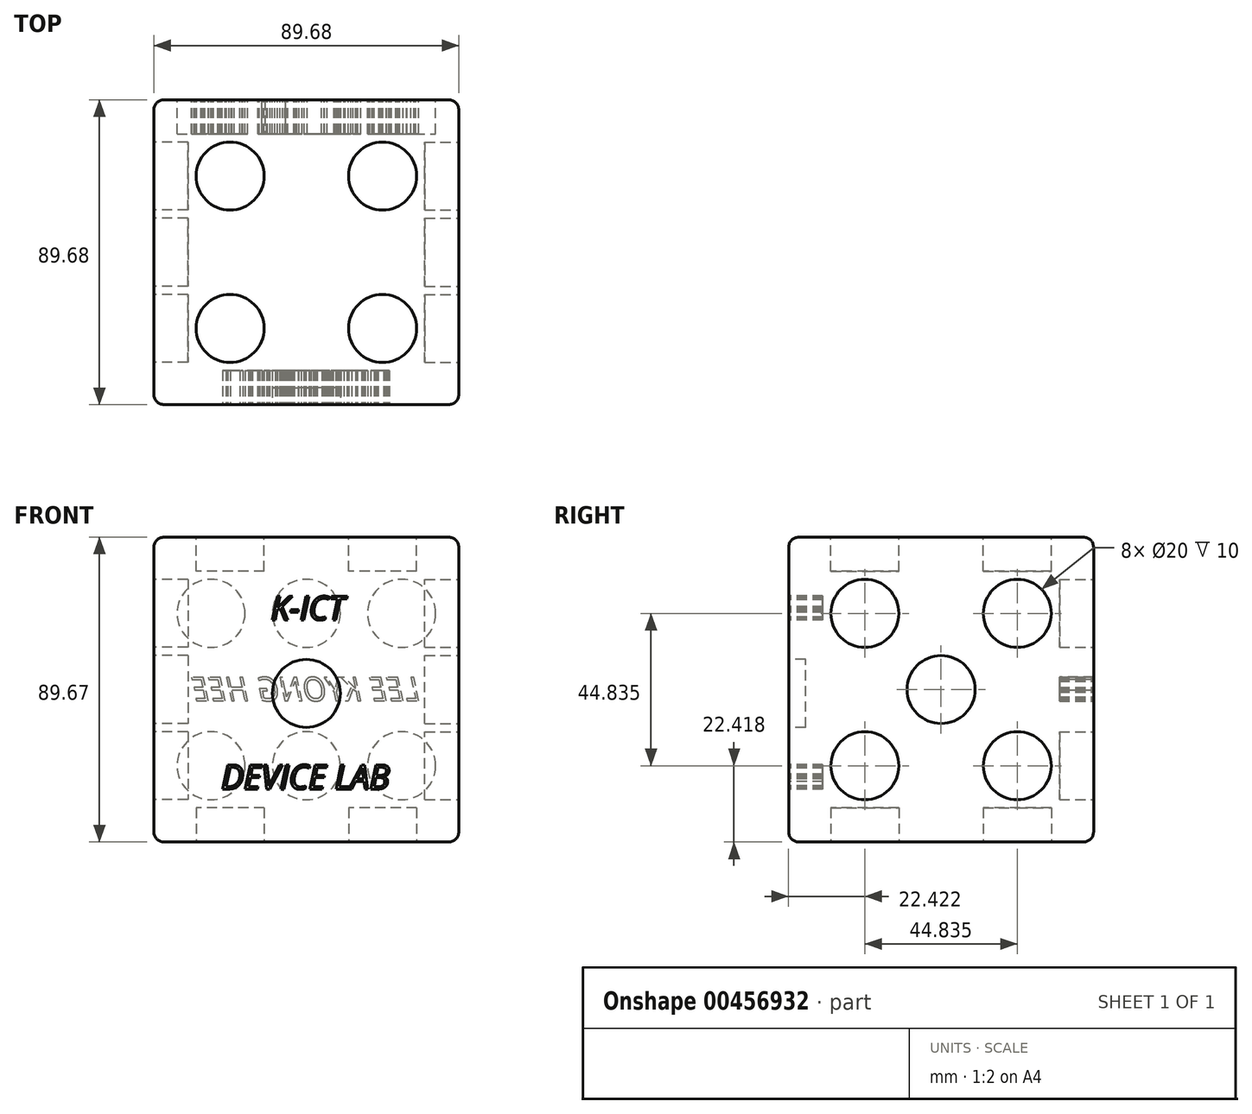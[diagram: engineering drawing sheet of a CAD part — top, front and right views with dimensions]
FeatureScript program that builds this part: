
annotation { "Feature Type Name" : "Feature", "Feature Type Description" : "" }
export const myFeature = defineFeature(function(context is Context, id is Id, definition is map)
    precondition{}
    {
        {
            var Q0;
            Q0=qCreatedBy(makeId("Top.planeOp"),FACE);
            var sketch = newSketch(context, id + "F0", { "sketchPlane" : qUnion([Q0])});
            skCircle(sketch, "E0.cCircle", {"center": v(0, 0) * mm, "radius": 44.84 * mm, "construction": true});
            skLineSegment(sketch, "E0.0", {"start": v(44.84, 44.84) * mm, "end": v(44.84, -44.84) * mm});
            skLineSegment(sketch, "E0.1", {"start": v(44.84, -44.84) * mm, "end": v(-44.84, -44.84) * mm});
            skLineSegment(sketch, "E0.2", {"start": v(-44.84, -44.84) * mm, "end": v(-44.84, 44.84) * mm});
            skLineSegment(sketch, "E0.3", {"start": v(-44.84, 44.84) * mm, "end": v(44.84, 44.84) * mm});
            skPoint(sketch, "E0.0.midPoint", {"position": v(44.84, 0) * mm});
            skSolve(sketch);
        }
        {
            var Q0;
            Q0 = qSketchRegion(id + "F0", true);
            extrude(context, id + "F1", {"entities" : qUnion([Q0]), "depth" : 89.67 * mm});
        }
        {
            var Q0;
            Q0=makeQuery(id+"F1.opExtrude","SWEPT_FACE",FACE,{"disambiguationData":[OSD([sQuery(id+"F0.wireOp",EDGE,"E0.1")])]});
            var sketch = newSketch(context, id + "F2", { "sketchPlane" : qUnion([Q0])});
            skCircle(sketch, "E1", {"center": v(0, 43.73) * mm, "radius": 10 * mm});
            skPoint(sketch, "E1.centerSnap0", {"position": v(0, 89.67) * mm});
            skSolve(sketch);
        }
        {
            var Q0;
            Q0 = qSketchRegion(id + "F2", true);
            extrude(context, id + "F3", {"entities" : qUnion([Q0]), "operationType" : NewBodyOperationType.REMOVE, "oppositeDirection" : true, "depth" : 5 * mm});
        }
        {
            var Q0;
            Q0=qCreatedBy(makeId("Top.planeOp"),FACE);
            var sketch = newSketch(context, id + "F4", { "sketchPlane" : qUnion([Q0])});
            skLineSegment(sketch, "E2", {"start": v(-44.84, -44.84) * mm, "end": v(44.84, 44.84) * mm, "construction": true});
            skLineSegment(sketch, "E3", {"start": v(44.84, -44.84) * mm, "end": v(-44.84, 44.84) * mm, "construction": true});
            skLineSegment(sketch, "E4", {"start": v(0, -44.84) * mm, "end": v(0, 44.84) * mm, "construction": true});
            skLineSegment(sketch, "E5", {"start": v(-44.84, 0) * mm, "end": v(44.84, 0) * mm, "construction": true});
            skLineSegment(sketch, "E6", {"start": v(0, -44.84) * mm, "end": v(-44.84, 0) * mm, "construction": true});
            skLineSegment(sketch, "E7", {"start": v(44.84, 0) * mm, "end": v(0, 44.84) * mm, "construction": true});
            skLineSegment(sketch, "E8", {"start": v(-44.84, 0) * mm, "end": v(0, 44.84) * mm, "construction": true});
            skLineSegment(sketch, "E9", {"start": v(0, -44.84) * mm, "end": v(44.84, 0) * mm, "construction": true});
            skCircle(sketch, "E10", {"center": v(-22.42, -22.42) * mm, "radius": 10 * mm});
            skCircle(sketch, "E11", {"center": v(22.42, -22.42) * mm, "radius": 10 * mm});
            skCircle(sketch, "E12", {"center": v(-22.42, 22.42) * mm, "radius": 10 * mm});
            skCircle(sketch, "E13", {"center": v(22.42, 22.42) * mm, "radius": 10 * mm});
            skSolve(sketch);
        }
        {
            var Q0;
            Q0 = qSketchRegion(id + "F4", true);
            extrude(context, id + "F5", {"entities" : qUnion([Q0]), "operationType" : NewBodyOperationType.REMOVE, "depth" : 10 * mm});
        }
        {
            var Q0;
            Q0=makeQuery(id+"F1.opExtrude","SWEPT_FACE",FACE,{"disambiguationData":[OSD([sQuery(id+"F0.wireOp",EDGE,"E0.0")])]});
            var sketch = newSketch(context, id + "F6", { "sketchPlane" : qUnion([Q0])});
            skLineSegment(sketch, "E14", {"start": v(-44.84, 0) * mm, "end": v(44.84, 89.67) * mm, "construction": true});
            skLineSegment(sketch, "E15", {"start": v(-44.84, 89.67) * mm, "end": v(44.84, 0) * mm, "construction": true});
            skLineSegment(sketch, "E16", {"start": v(0, 0) * mm, "end": v(0, 89.67) * mm, "construction": true});
            skLineSegment(sketch, "E17", {"start": v(0, 44.84) * mm, "end": v(44.84, 44.84) * mm, "construction": true});
            skLineSegment(sketch, "E18", {"start": v(0, 44.84) * mm, "end": v(-44.84, 44.84) * mm, "construction": true});
            skLineSegment(sketch, "E19", {"start": v(0, 89.67) * mm, "end": v(-44.84, 44.83) * mm, "construction": true});
            skLineSegment(sketch, "E20", {"start": v(0, 89.67) * mm, "end": v(44.84, 44.84) * mm, "construction": true});
            skLineSegment(sketch, "E21", {"start": v(44.84, 44.84) * mm, "end": v(0, 0) * mm, "construction": true});
            skLineSegment(sketch, "E22", {"start": v(0, 0) * mm, "end": v(-44.84, 44.84) * mm, "construction": true});
            skCircle(sketch, "E23", {"center": v(-22.42, 67.25) * mm, "radius": 10 * mm});
            skCircle(sketch, "E24", {"center": v(22.42, 67.25) * mm, "radius": 10 * mm});
            skCircle(sketch, "E25", {"center": v(0, 44.84) * mm, "radius": 10 * mm});
            skCircle(sketch, "E26", {"center": v(-22.42, 22.42) * mm, "radius": 10 * mm});
            skCircle(sketch, "E27", {"center": v(22.42, 22.42) * mm, "radius": 10 * mm});
            skPoint(sketch, "E28", {"position": v(44.84, 44.84) * mm});
            skSolve(sketch);
        }
        {
            var Q0;
            Q0 = qSketchRegion(id + "F6", true);
            extrude(context, id + "F7", {"entities" : qUnion([Q0]), "operationType" : NewBodyOperationType.REMOVE, "oppositeDirection" : true, "depth" : 10 * mm});
        }
        {
            var Q0;
            Q0=makeQuery(id+"F1.opExtrude","SWEPT_FACE",FACE,{"disambiguationData":[OSD([sQuery(id+"F0.wireOp",EDGE,"E0.2")])]});
            var sketch = newSketch(context, id + "F8", { "sketchPlane" : qUnion([Q0])});
            skLineSegment(sketch, "E29", {"start": v(-44.84, 0) * mm, "end": v(44.84, 89.67) * mm, "construction": true});
            skLineSegment(sketch, "E30", {"start": v(0, 0) * mm, "end": v(0, 89.67) * mm, "construction": true});
            skLineSegment(sketch, "E31", {"start": v(0, 44.84) * mm, "end": v(-44.84, 44.84) * mm, "construction": true});
            skLineSegment(sketch, "E32", {"start": v(0, 44.84) * mm, "end": v(44.84, 44.84) * mm, "construction": true});
            skLineSegment(sketch, "E33", {"start": v(44.84, 0) * mm, "end": v(-44.84, 89.67) * mm, "construction": true});
            skLineSegment(sketch, "E34", {"start": v(0, 0) * mm, "end": v(-44.84, 44.84) * mm, "construction": true});
            skLineSegment(sketch, "E35", {"start": v(44.84, 44.83) * mm, "end": v(0, 89.67) * mm, "construction": true});
            skCircle(sketch, "E36", {"center": v(0, 44.84) * mm, "radius": 10 * mm});
            skCircle(sketch, "E37", {"center": v(-22.42, 22.42) * mm, "radius": 10 * mm});
            skCircle(sketch, "E38", {"center": v(22.42, 67.25) * mm, "radius": 10 * mm});
            skSolve(sketch);
        }
        {
            var Q0;
            Q0 = qSketchRegion(id + "F8", true);
            extrude(context, id + "F9", {"entities" : qUnion([Q0]), "operationType" : NewBodyOperationType.REMOVE, "oppositeDirection" : true, "depth" : 10 * mm});
        }
        {
            var Q0;
            Q0=makeQuery(id+"F1.opExtrude","CAP_FACE",FACE,{"disambiguationData":[OSD([sQuery(id+"F0.wireOp",EDGE,"E0.0"),sQuery(id+"F0.wireOp",EDGE,"E0.1"),sQuery(id+"F0.wireOp",EDGE,"E0.2"),sQuery(id+"F0.wireOp",EDGE,"E0.3")])],"isStart":false});
            var sketch = newSketch(context, id + "F10", { "sketchPlane" : qUnion([Q0])});
            skLineSegment(sketch, "E39", {"start": v(0, -44.84) * mm, "end": v(0, 44.84) * mm, "construction": true});
            skLineSegment(sketch, "E40", {"start": v(-44.84, -44.84) * mm, "end": v(44.84, 44.84) * mm, "construction": true});
            skLineSegment(sketch, "E41", {"start": v(44.84, -44.84) * mm, "end": v(-44.84, 44.84) * mm, "construction": true});
            skLineSegment(sketch, "E42", {"start": v(44.84, 0) * mm, "end": v(-44.84, 0) * mm, "construction": true});
            skLineSegment(sketch, "E43", {"start": v(0, -44.84) * mm, "end": v(44.84, 0) * mm, "construction": true});
            skLineSegment(sketch, "E44", {"start": v(44.84, 0) * mm, "end": v(0, 44.84) * mm, "construction": true});
            skLineSegment(sketch, "E45", {"start": v(0, -44.84) * mm, "end": v(-44.84, 0) * mm, "construction": true});
            skLineSegment(sketch, "E46", {"start": v(-44.84, 0) * mm, "end": v(0, 44.84) * mm, "construction": true});
            skCircle(sketch, "E47", {"center": v(22.42, -22.42) * mm, "radius": 10 * mm});
            skCircle(sketch, "E48", {"center": v(-22.42, -22.42) * mm, "radius": 10 * mm});
            skCircle(sketch, "E49", {"center": v(22.42, 22.42) * mm, "radius": 10 * mm});
            skCircle(sketch, "E50", {"center": v(-22.42, 22.42) * mm, "radius": 10 * mm});
            skSolve(sketch);
        }
        {
            var Q0;
            Q0 = qSketchRegion(id + "F10", true);
            extrude(context, id + "F11", {"entities" : qUnion([Q0]), "operationType" : NewBodyOperationType.REMOVE, "oppositeDirection" : true, "depth" : 10 * mm});
        }
        {
            var Q0;
            Q0=makeQuery(id+"F1.opExtrude","SWEPT_FACE",FACE,{"disambiguationData":[OSD([sQuery(id+"F0.wireOp",EDGE,"E0.3")])]});
            var sketch = newSketch(context, id + "F12", { "sketchPlane" : qUnion([Q0])});
            skLineSegment(sketch, "E51", {"start": v(-44.84, 0) * mm, "end": v(44.84, 89.67) * mm, "construction": true});
            skLineSegment(sketch, "E52", {"start": v(-44.84, 89.67) * mm, "end": v(44.84, 0) * mm, "construction": true});
            skLineSegment(sketch, "E53", {"start": v(0, 44.84) * mm, "end": v(44.84, 44.84) * mm, "construction": true});
            skLineSegment(sketch, "E54", {"start": v(0, 44.84) * mm, "end": v(-44.84, 44.84) * mm, "construction": true});
            skLineSegment(sketch, "E55", {"start": v(-44.84, 44.84) * mm, "end": v(0, 0) * mm, "construction": true});
            skLineSegment(sketch, "E56", {"start": v(0, 0) * mm, "end": v(44.84, 44.84) * mm, "construction": true});
            skLineSegment(sketch, "E57", {"start": v(0, 0) * mm, "end": v(0, 89.67) * mm, "construction": true});
            skLineSegment(sketch, "E58", {"start": v(0, 89.67) * mm, "end": v(-44.84, 44.83) * mm, "construction": true});
            skLineSegment(sketch, "E59", {"start": v(0, 89.67) * mm, "end": v(44.84, 44.83) * mm, "construction": true});
            skLineSegment(sketch, "E60", {"start": v(-22.42, 22.42) * mm, "end": v(44.84, 22.42) * mm, "construction": true});
            skLineSegment(sketch, "E61", {"start": v(-44.84, 22.42) * mm, "end": v(-22.42, 22.42) * mm, "construction": true});
            skLineSegment(sketch, "E62", {"start": v(-22.42, 67.25) * mm, "end": v(44.84, 67.25) * mm, "construction": true});
            skLineSegment(sketch, "E63", {"start": v(-22.42, 67.25) * mm, "end": v(-44.84, 67.25) * mm, "construction": true});
            skLineSegment(sketch, "E64", {"start": v(-22.42, 22.42) * mm, "end": v(-22.42, 89.67) * mm, "construction": true});
            skLineSegment(sketch, "E65", {"start": v(-22.42, 22.42) * mm, "end": v(-22.42, 0) * mm, "construction": true});
            skLineSegment(sketch, "E66", {"start": v(-44.84, 22.42) * mm, "end": v(-22.42, 0) * mm, "construction": true});
            skLineSegment(sketch, "E67", {"start": v(22.42, 22.42) * mm, "end": v(22.42, 89.67) * mm, "construction": true});
            skLineSegment(sketch, "E68", {"start": v(22.42, 22.42) * mm, "end": v(22.42, 0) * mm, "construction": true});
            skLineSegment(sketch, "E69", {"start": v(22.42, 0) * mm, "end": v(44.84, 22.42) * mm, "construction": true});
            skLineSegment(sketch, "E70", {"start": v(44.84, 67.25) * mm, "end": v(22.42, 89.67) * mm, "construction": true});
            skLineSegment(sketch, "E71", {"start": v(-22.42, 89.67) * mm, "end": v(-44.84, 67.25) * mm, "construction": true});
            skLineSegment(sketch, "E72", {"start": v(-33.63, 78.46) * mm, "end": v(33.63, 78.46) * mm, "construction": true});
            skLineSegment(sketch, "E73", {"start": v(33.63, 78.46) * mm, "end": v(33.63, 11.2) * mm, "construction": true});
            skLineSegment(sketch, "E74", {"start": v(33.63, 11.2) * mm, "end": v(-33.63, 11.2) * mm, "construction": true});
            skLineSegment(sketch, "E75", {"start": v(-33.63, 11.2) * mm, "end": v(-33.63, 78.46) * mm, "construction": true});
            skCircle(sketch, "E76", {"center": v(0, 67.25) * mm, "radius": 10 * mm});
            skLineSegment(sketch, "E77", {"start": v(33.63, 67.25) * mm, "end": v(22.42, 78.46) * mm});
            skLineSegment(sketch, "E78", {"start": v(-22.42, 78.46) * mm, "end": v(-33.63, 67.25) * mm});
            skLineSegment(sketch, "E79", {"start": v(-28.02, 72.86) * mm, "end": v(-28.02, 0) * mm, "construction": true});
            skLineSegment(sketch, "E80", {"start": v(28.02, 72.86) * mm, "end": v(28.02, 0) * mm, "construction": true});
            skCircle(sketch, "E81", {"center": v(28.02, 67.25) * mm, "radius": 10 * mm});
            skCircle(sketch, "E82", {"center": v(-28.02, 67.25) * mm, "radius": 10 * mm});
            skCircle(sketch, "E83.MirrorC", {"center": v(28.02, 22.42) * mm, "radius": 10 * mm});
            skCircle(sketch, "E84.MirrorC", {"center": v(0, 22.42) * mm, "radius": 10 * mm});
            skCircle(sketch, "E85.MirrorC", {"center": v(-28.02, 22.42) * mm, "radius": 10 * mm});
            skSolve(sketch);
        }
        {
            var Q0;
            Q0 = qSketchRegion(id + "F12", true);
            extrude(context, id + "F13", {"entities" : qUnion([Q0]), "operationType" : NewBodyOperationType.REMOVE, "oppositeDirection" : true, "depth" : 10 * mm});
        }
        {
            var Q0;
            Q0=makeQuery(id+"F1.opExtrude","CAP_EDGE",EDGE,{"disambiguationData":[OSD([sQuery(id+"F0.wireOp",EDGE,"E0.2")])],"isStart":true});
            var Q1;
            Q1=makeQuery(id+"F1.opExtrude","CAP_EDGE",EDGE,{"disambiguationData":[OSD([sQuery(id+"F0.wireOp",EDGE,"E0.1")])],"isStart":true});
            var Q2;
            Q2=makeQuery(id+"F1.opExtrude","CAP_EDGE",EDGE,{"disambiguationData":[OSD([sQuery(id+"F0.wireOp",EDGE,"E0.0")])],"isStart":true});
            var Q3;
            Q3=makeQuery(id+"F1.opExtrude","CAP_EDGE",EDGE,{"disambiguationData":[OSD([sQuery(id+"F0.wireOp",EDGE,"E0.3")])],"isStart":true});
            var Q4;
            Q4=makeQuery(id+"F1.opExtrude","SWEPT_EDGE",EDGE,{"disambiguationData":[OSD([sQuery(id+"F0.wireOp",EDGE,"E0.1"),sQuery(id+"F0.wireOp",EDGE,"E0.2")])]});
            var Q5;
            Q5=makeQuery(id+"F1.opExtrude","SWEPT_EDGE",EDGE,{"disambiguationData":[OSD([sQuery(id+"F0.wireOp",EDGE,"E0.2"),sQuery(id+"F0.wireOp",EDGE,"E0.3")])]});
            var Q6;
            Q6=makeQuery(id+"F1.opExtrude","SWEPT_EDGE",EDGE,{"disambiguationData":[OSD([sQuery(id+"F0.wireOp",EDGE,"E0.0"),sQuery(id+"F0.wireOp",EDGE,"E0.1")])]});
            var Q7;
            Q7=makeQuery(id+"F1.opExtrude","CAP_EDGE",EDGE,{"disambiguationData":[OSD([sQuery(id+"F0.wireOp",EDGE,"E0.1")])],"isStart":false});
            var Q8;
            Q8=makeQuery(id+"F1.opExtrude","CAP_EDGE",EDGE,{"disambiguationData":[OSD([sQuery(id+"F0.wireOp",EDGE,"E0.2")])],"isStart":false});
            var Q9;
            Q9=makeQuery(id+"F1.opExtrude","SWEPT_EDGE",EDGE,{"disambiguationData":[OSD([sQuery(id+"F0.wireOp",EDGE,"E0.0"),sQuery(id+"F0.wireOp",EDGE,"E0.3")])]});
            var Q10;
            Q10=makeQuery(id+"F1.opExtrude","CAP_EDGE",EDGE,{"disambiguationData":[OSD([sQuery(id+"F0.wireOp",EDGE,"E0.3")])],"isStart":false});
            var Q11;
            Q11=makeQuery(id+"F1.opExtrude","CAP_EDGE",EDGE,{"disambiguationData":[OSD([sQuery(id+"F0.wireOp",EDGE,"E0.0")])],"isStart":false});
            fillet(context, id + "F14", {"entities" : qUnion([Q0, Q1, Q2, Q3, Q4, Q5, Q6, Q7, Q8, Q9, Q10, Q11]), "radius" : 3 * mm, "tangentPropagation" : true, "allowEdgeOverflow" : false});
        }
        {
            var Q0;
            Q0=makeQuery(id+"F1.opExtrude","SWEPT_FACE",FACE,{"disambiguationData":[OSD([sQuery(id+"F0.wireOp",EDGE,"E0.3")])]});
            var sketch = newSketch(context, id + "F15", { "sketchPlane" : qUnion([Q0])});
            skText(sketch, "E86", { "text": "LEE KYONG HEE", "fontName": "OpenSans-Italic.ttf"});
            const initialGuessF15  = {"E86": [-0.03347, 0.0415, 1, 0, 0.007]};
            skSetInitialGuess(sketch, initialGuessF15);
            skSolve(sketch);
        }
        {
            var Q0;
            Q0 = qSketchRegion(id + "F15", true);
            extrude(context, id + "F16", {"entities" : qUnion([Q0]), "operationType" : NewBodyOperationType.REMOVE, "oppositeDirection" : true, "depth" : 10 * mm});
        }
        {
            var Q0;
            Q0=makeQuery(id+"F1.opExtrude","SWEPT_FACE",FACE,{"disambiguationData":[OSD([sQuery(id+"F0.wireOp",EDGE,"E0.1")])]});
            var sketch = newSketch(context, id + "F17", { "sketchPlane" : qUnion([Q0])});
            skText(sketch, "E87", { "text": "DEVICE LAB", "fontName": "OpenSans-Italic.ttf"});
            skText(sketch, "E88", { "text": "K-ICT", "fontName": "OpenSans-Italic.ttf"});
            const initialGuessF17  = {"E87": [-0.025, 0.01556, 1, 0, 0.00715], "E88": [-0.0104, 0.06533, 1, 0, 0.007]};
            skSetInitialGuess(sketch, initialGuessF17);
            skSolve(sketch);
        }
        {
            var Q0;
            Q0 = qSketchRegion(id + "F17", true);
            extrude(context, id + "F18", {"entities" : qUnion([Q0]), "operationType" : NewBodyOperationType.REMOVE, "oppositeDirection" : true, "depth" : 10 * mm});
        }
    });
